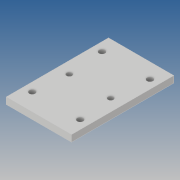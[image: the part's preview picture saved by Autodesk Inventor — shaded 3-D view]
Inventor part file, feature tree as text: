
AUTODESK INVENTOR PART (.ipt)
format: ipt  version: 2019 (Build 230136000, 136)  size: 103,936 bytes
history: native  units: mm
features: sketch x3, hole x2, extrude x1
ambient origin geometry x8: Origin, YZ Plane, XZ Plane, XY Plane, X Axis, Y Axis, Z Axis, Center Point
bodies: Solide1 (feature_tree)
feature tree (6):
  extrude  "Extrusion1"  Depth=60.0mm
  hole  "Perçage1"  [1 undecoded]
  hole  "Perçage2"  [1 undecoded]
  sketch  "Esquisse1"
  sketch  "Esquisse2"
  sketch  "Esquisse4"
note: 2 required parameter values undecoded (feature->parameter linkage not recoverable at this tier; creation-order binding heuristic only, values carry confidence <= 0.55)
